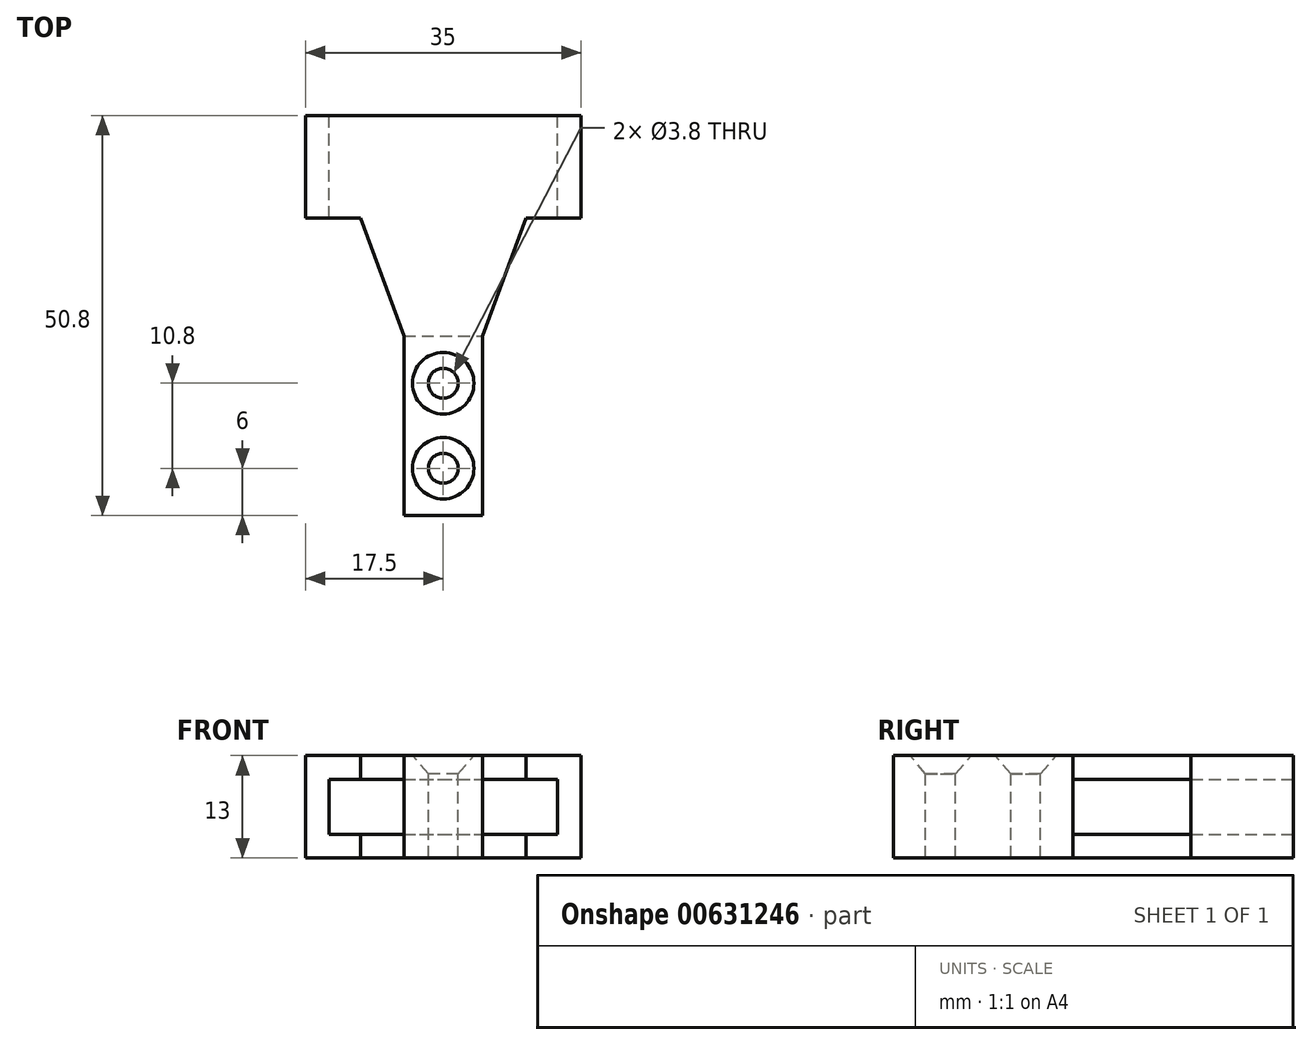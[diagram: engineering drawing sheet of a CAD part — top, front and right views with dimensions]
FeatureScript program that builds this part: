
annotation { "Feature Type Name" : "Feature", "Feature Type Description" : "" }
export const myFeature = defineFeature(function(context is Context, id is Id, definition is map)
    precondition{}
    {
        {
            var Q0;
            Q0=qCreatedBy(makeId("Top.planeOp"),FACE);
            var sketch = newSketch(context, id + "F0", { "sketchPlane" : qUnion([Q0])});
            skLineSegment(sketch, "E0.bottom", {"start": v(-17.5, 25.4) * mm, "end": v(17.5, 25.4) * mm});
            skLineSegment(sketch, "E0.top", {"start": v(-17.5, -25.4) * mm, "end": v(17.5, -25.4) * mm});
            skLineSegment(sketch, "E0.left", {"start": v(-17.5, 25.4) * mm, "end": v(-17.5, -25.4) * mm});
            skLineSegment(sketch, "E0.right", {"start": v(17.5, 25.4) * mm, "end": v(17.5, -25.4) * mm});
            skPoint(sketch, "E0.middle", {"position": v(0, 0) * mm});
            skSolve(sketch);
        }
        {
            var Q0;
            Q0=makeQuery(id+"F0.imprint","IMPRINT",FACE,{"disambiguationData":[TD([[makeQuery(id+"F0.imprint","IMPRINT",EDGE,{"derivedFrom":sQuery(id+"F0.wireOp",EDGE,"E0.bottom")}),-1.0]])]});
            extrude(context, id + "F1", {"entities" : qUnion([Q0]), "depth" : 13 * mm, "offsetDistance" : 25 * mm});
        }
        {
            var Q0;
            Q0=makeQuery(id+"F1.opExtrude","SWEPT_FACE",FACE,{"disambiguationData":[OSD([sQuery(id+"F0.wireOp",EDGE,"E0.bottom")])]});
            var sketch = newSketch(context, id + "F2", { "sketchPlane" : qUnion([Q0])});
            skPoint(sketch, "E1", {"position": v(14.5, 10) * mm});
            skPoint(sketch, "E2", {"position": v(-14.5, 3) * mm});
            skLineSegment(sketch, "E3.bottom", {"start": v(14.5, 10) * mm, "end": v(-14.5, 10) * mm});
            skLineSegment(sketch, "E3.top", {"start": v(14.5, 3) * mm, "end": v(-14.5, 3) * mm});
            skLineSegment(sketch, "E3.left", {"start": v(14.5, 10) * mm, "end": v(14.5, 3) * mm});
            skLineSegment(sketch, "E3.right", {"start": v(-14.5, 10) * mm, "end": v(-14.5, 3) * mm});
            skSolve(sketch);
        }
        {
            var Q0;
            Q0=makeQuery(id+"F2.imprint","IMPRINT",FACE,{"disambiguationData":[TD([[makeQuery(id+"F2.imprint","IMPRINT",EDGE,{"derivedFrom":sQuery(id+"F2.wireOp",EDGE,"E3.bottom")}),1.0]])]});
            extrude(context, id + "F3", {"entities" : qUnion([Q0]), "operationType" : NewBodyOperationType.REMOVE, "oppositeDirection" : true, "depth" : 28 * mm, "offsetDistance" : 25 * mm});
        }
        {
            var Q0;
            Q0=makeQuery(id+"F1.opExtrude","SWEPT_FACE",FACE,{"disambiguationData":[OSD([sQuery(id+"F0.wireOp",EDGE,"E0.right")])]});
            var sketch = newSketch(context, id + "F4", { "sketchPlane" : qUnion([Q0])});
            skPoint(sketch, "E4", {"position": v(12.4, 10) * mm});
            skPoint(sketch, "E5", {"position": v(-2.6, 3) * mm});
            skLineSegment(sketch, "E6.bottom", {"start": v(-2.6, 3) * mm, "end": v(12.4, 3) * mm});
            skLineSegment(sketch, "E6.top", {"start": v(-2.6, 10) * mm, "end": v(12.4, 10) * mm});
            skLineSegment(sketch, "E6.left", {"start": v(-2.6, 3) * mm, "end": v(-2.6, 10) * mm});
            skLineSegment(sketch, "E6.right", {"start": v(12.4, 3) * mm, "end": v(12.4, 10) * mm});
            skSolve(sketch);
        }
        {
            var Q0;
            Q0=makeQuery(id+"F4.imprint","IMPRINT",FACE,{"disambiguationData":[TD([[makeQuery(id+"F4.imprint","IMPRINT",EDGE,{"derivedFrom":sQuery(id+"F4.wireOp",EDGE,"E6.bottom")}),1.0]])]});
            extrude(context, id + "F5", {"entities" : qUnion([Q0]), "operationType" : NewBodyOperationType.REMOVE, "endBound" : BoundingType.THROUGH_ALL, "oppositeDirection" : true, "depth" : 25 * mm, "offsetDistance" : 25 * mm});
        }
        {
            var Q0;
            Q0=makeQuery(id+"F1.opExtrude","CAP_FACE",FACE,{"disambiguationData":[OSD([sQuery(id+"F0.wireOp",EDGE,"E0.bottom"),sQuery(id+"F0.wireOp",EDGE,"E0.top"),sQuery(id+"F0.wireOp",EDGE,"E0.left"),sQuery(id+"F0.wireOp",EDGE,"E0.right")])],"isStart":false});
            var sketch = newSketch(context, id + "F6", { "sketchPlane" : qUnion([Q0])});
            skPoint(sketch, "E7", {"position": v(17.5, 12.4) * mm});
            skPoint(sketch, "E8", {"position": v(10.5, 12.4) * mm});
            skPoint(sketch, "E9", {"position": v(-17.5, 12.4) * mm});
            skPoint(sketch, "E10", {"position": v(-10.5, 12.4) * mm});
            skPoint(sketch, "E11", {"position": v(0, 25.4) * mm});
            skLineSegment(sketch, "E12", {"start": v(0, 25.4) * mm, "end": v(0, -2.6) * mm});
            skPoint(sketch, "E13", {"position": v(-5, -2.6) * mm});
            skPoint(sketch, "E14", {"position": v(5, -2.6) * mm});
            skLineSegment(sketch, "E15", {"start": v(17.5, 12.4) * mm, "end": v(10.5, 12.4) * mm});
            skLineSegment(sketch, "E16", {"start": v(5, -2.6) * mm, "end": v(10.5, 12.4) * mm});
            skLineSegment(sketch, "E17", {"start": v(-5, -2.6) * mm, "end": v(-10.5, 12.4) * mm});
            skLineSegment(sketch, "E18", {"start": v(-17.5, 12.4) * mm, "end": v(-10.5, 12.4) * mm});
            skLineSegment(sketch, "E19", {"start": v(-17.5, -2.6) * mm, "end": v(-17.5, 12.4) * mm});
            skLineSegment(sketch, "E20", {"start": v(17.5, -2.6) * mm, "end": v(17.5, 12.4) * mm});
            skLineSegment(sketch, "E21", {"start": v(-5, -2.6) * mm, "end": v(-5, -25.4) * mm});
            skLineSegment(sketch, "E22", {"start": v(5, -2.6) * mm, "end": v(5, -25.4) * mm});
            skSolve(sketch);
        }
        {
            var Q0;
            Q0=makeQuery(id+"F6.imprint","IMPRINT",FACE,{"disambiguationData":[TD([[makeQuery(id+"F6.imprint","IMPRINT",EDGE,{"derivedFrom":sQuery(id+"F6.wireOp",EDGE,"E17")}),1.0]])]});
            var Q1;
            Q1=makeQuery(id+"F6.imprint","IMPRINT",FACE,{"disambiguationData":[TD([[makeQuery(id+"F6.imprint","IMPRINT",EDGE,{"derivedFrom":sQuery(id+"F6.wireOp",EDGE,"E15")}),1.0]])]});
            extrude(context, id + "F7", {"entities" : qUnion([Q0, Q1]), "operationType" : NewBodyOperationType.REMOVE, "endBound" : BoundingType.THROUGH_ALL, "oppositeDirection" : true, "depth" : 25 * mm, "offsetDistance" : 25 * mm});
        }
        {
            var Q0;
            Q0=makeQuery(id+"F1.opExtrude","CAP_FACE",FACE,{"disambiguationData":[OSD([sQuery(id+"F0.wireOp",EDGE,"E0.bottom"),sQuery(id+"F0.wireOp",EDGE,"E0.top"),sQuery(id+"F0.wireOp",EDGE,"E0.left"),sQuery(id+"F0.wireOp",EDGE,"E0.right")])],"isStart":false});
            var sketch = newSketch(context, id + "F8", { "sketchPlane" : qUnion([Q0])});
            skLineSegment(sketch, "E23", {"start": v(5, -2.6) * mm, "end": v(-5, -2.6) * mm});
            skPoint(sketch, "E24", {"position": v(0, -8.6) * mm});
            skPoint(sketch, "E25", {"position": v(0, -19.4) * mm});
            skSolve(sketch);
        }
        {
            var Q0;
            Q0=sQuery(id+"F8.wireOp",VERTEX,"E24");
            var Q1;
            Q1=sQuery(id+"F8.wireOp",VERTEX,"E25");
            var Q2;
            Q2=makeQuery(id+"F1.opExtrude","SWEPT_BODY",BODY,{"disambiguationData":[OSD([sQuery(id+"F0.wireOp",EDGE,"E0.bottom"),sQuery(id+"F0.wireOp",EDGE,"E0.top"),sQuery(id+"F0.wireOp",EDGE,"E0.left"),sQuery(id+"F0.wireOp",EDGE,"E0.right")])]});
            hole(context, id + "F9", {"style" : HoleStyle.C_SINK, "endStyle" : HoleEndStyle.THROUGH, "standardTappedOrClearance" : lookupTablePath({ "standard" : "ANSI", "fit" : "Normal (ASME)", "size" : "#6", "type" : "Clearance" }), "standardBlindInLast" : lookupTablePath({ "fit" : "Free", "standard" : "ANSI", "size" : "#6", "type" : "Clearance" }), "holeDiameter" : 3.8 * mm, "cSinkDiameter" : 7.8 * mm, "cSinkAngle" : 82 * degree, "majorDiameter" : 5 * mm, "isTappedThrough" : true, "tappedDepth" : 1 * mm, "tapClearance" : 3, "locations" : qUnion([Q0, Q1]), "scope" : qUnion([Q2])});
        }
    });
